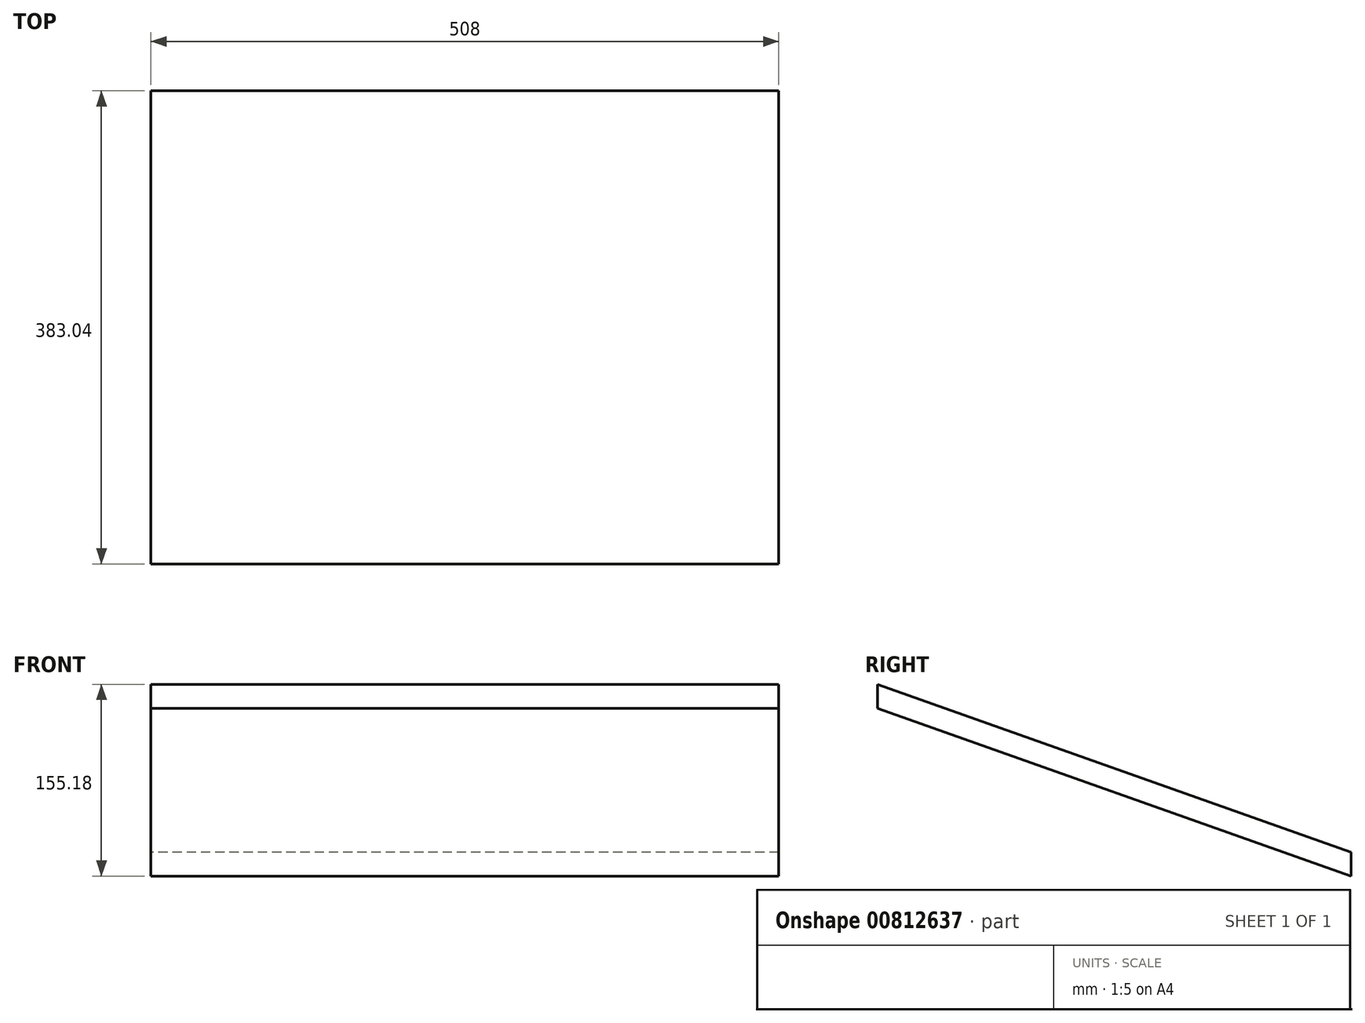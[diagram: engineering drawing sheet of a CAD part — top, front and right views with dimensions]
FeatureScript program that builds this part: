
annotation { "Feature Type Name" : "Feature", "Feature Type Description" : "" }
export const myFeature = defineFeature(function(context is Context, id is Id, definition is map)
    precondition{}
    {
        {
            var Q0;
            Q0=qCreatedBy(makeId("Right.planeOp"),FACE);
            var sketch = newSketch(context, id + "F0", { "sketchPlane" : qUnion([Q0])});
            skLineSegment(sketch, "E0", {"start": v(-152.72, -69.6) * mm, "end": v(133.82, -69.6) * mm});
            skLineSegment(sketch, "E1", {"start": v(133.82, -69.6) * mm, "end": v(-152.72, 32) * mm});
            skLineSegment(sketch, "E2", {"start": v(-152.72, 32) * mm, "end": v(-152.72, -69.6) * mm});
            skSolve(sketch);
        }
        {
            var Q0;
            Q0=qCreatedBy(makeId("Right.planeOp"),FACE);
            var sketch = newSketch(context, id + "F1", { "sketchPlane" : qUnion([Q0])});
            skLineSegment(sketch, "E3", {"start": v(-79.72, 30.45) * mm, "end": v(-79.72, 11.08) * mm});
            skLineSegment(sketch, "E4", {"start": v(-79.72, 11.08) * mm, "end": v(303.32, -124.73) * mm});
            skLineSegment(sketch, "E5", {"start": v(303.32, -124.73) * mm, "end": v(303.32, -105.36) * mm});
            skLineSegment(sketch, "E6", {"start": v(303.32, -105.36) * mm, "end": v(-79.72, 30.45) * mm});
            skSolve(sketch);
        }
        {
            var Q0;
            Q0=qSketchRegion(id+"F1",true);
            extrude(context, id + "F2", {"entities" : qUnion([Q0]), "depth" : 508 * mm, "offsetDistance" : 25.4 * mm});
        }
    });
